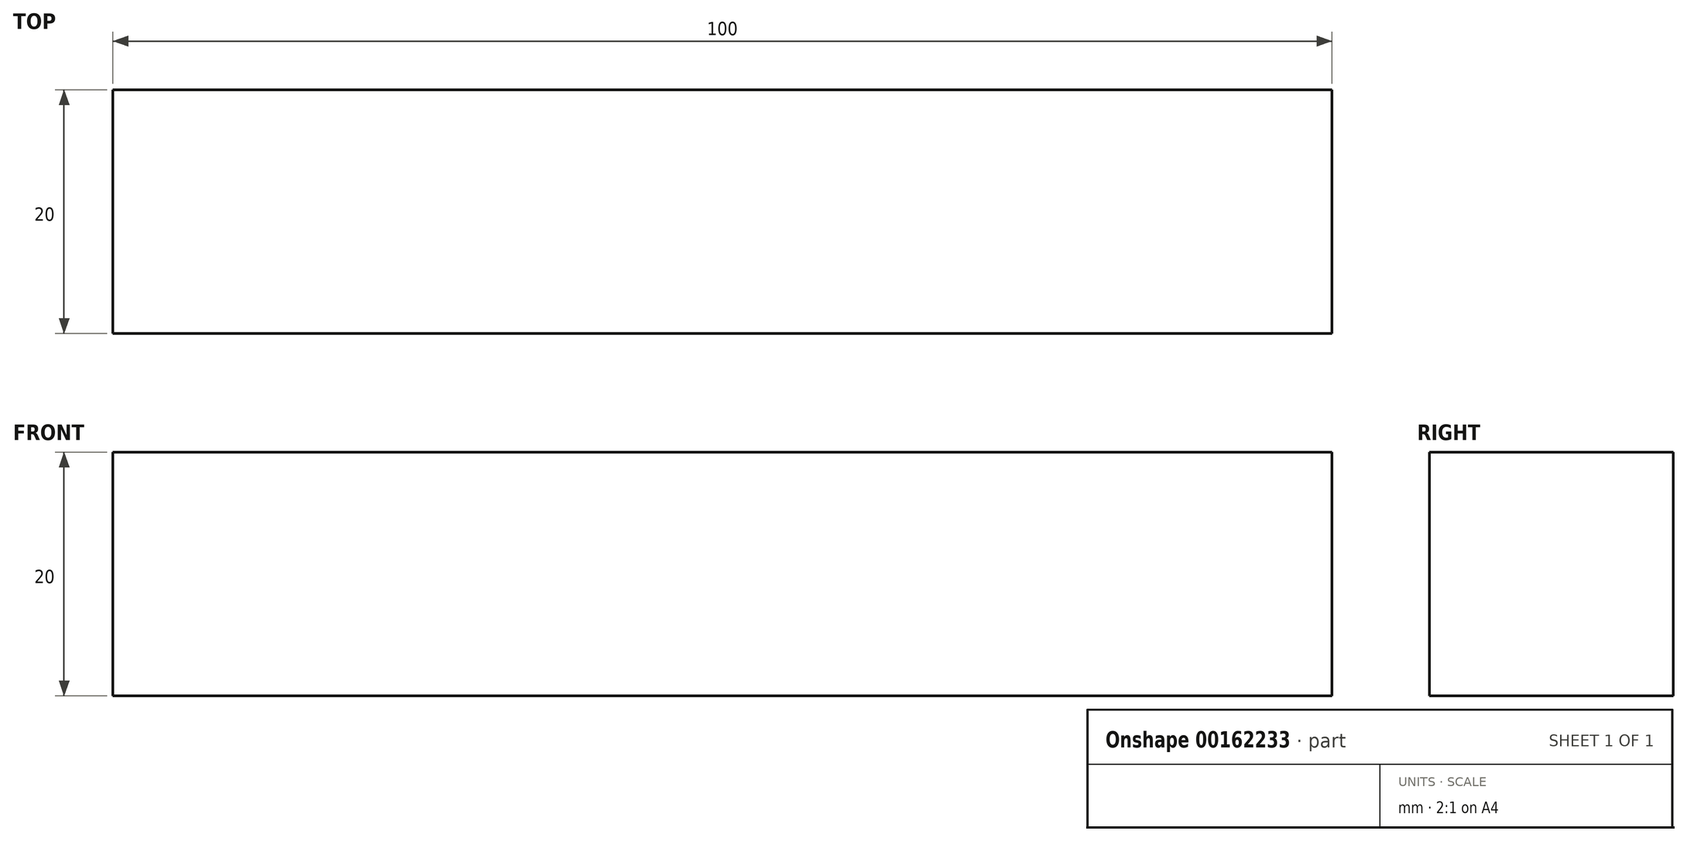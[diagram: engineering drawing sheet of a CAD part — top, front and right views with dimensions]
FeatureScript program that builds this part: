
annotation { "Feature Type Name" : "Feature", "Feature Type Description" : "" }
export const myFeature = defineFeature(function(context is Context, id is Id, definition is map)
    precondition{}
    {
        {
            var Q0;
            Q0=qCreatedBy(makeId("Top.planeOp"),FACE);
            var sketch = newSketch(context, id + "F0", { "sketchPlane" : qUnion([Q0])});
            skLineSegment(sketch, "E0.bottom", {"start": v(0, 0) * mm, "end": v(-100, 0) * mm});
            skLineSegment(sketch, "E0.top", {"start": v(0, 20) * mm, "end": v(-100, 20) * mm});
            skLineSegment(sketch, "E0.left", {"start": v(0, 0) * mm, "end": v(0, 20) * mm});
            skLineSegment(sketch, "E0.right", {"start": v(-100, 0) * mm, "end": v(-100, 20) * mm});
            skSolve(sketch);
        }
        {
            var Q0;
            Q0=makeQuery(id+"F0.imprint","IMPRINT",FACE,{"disambiguationData":[TD([[makeQuery(id+"F0.imprint","IMPRINT",EDGE,{"derivedFrom":sQuery(id+"F0.wireOp",EDGE,"E0.bottom")}),-1.0]])]});
            extrude(context, id + "F1", {"entities" : qUnion([Q0]), "depth" : 20 * mm});
        }
    });
